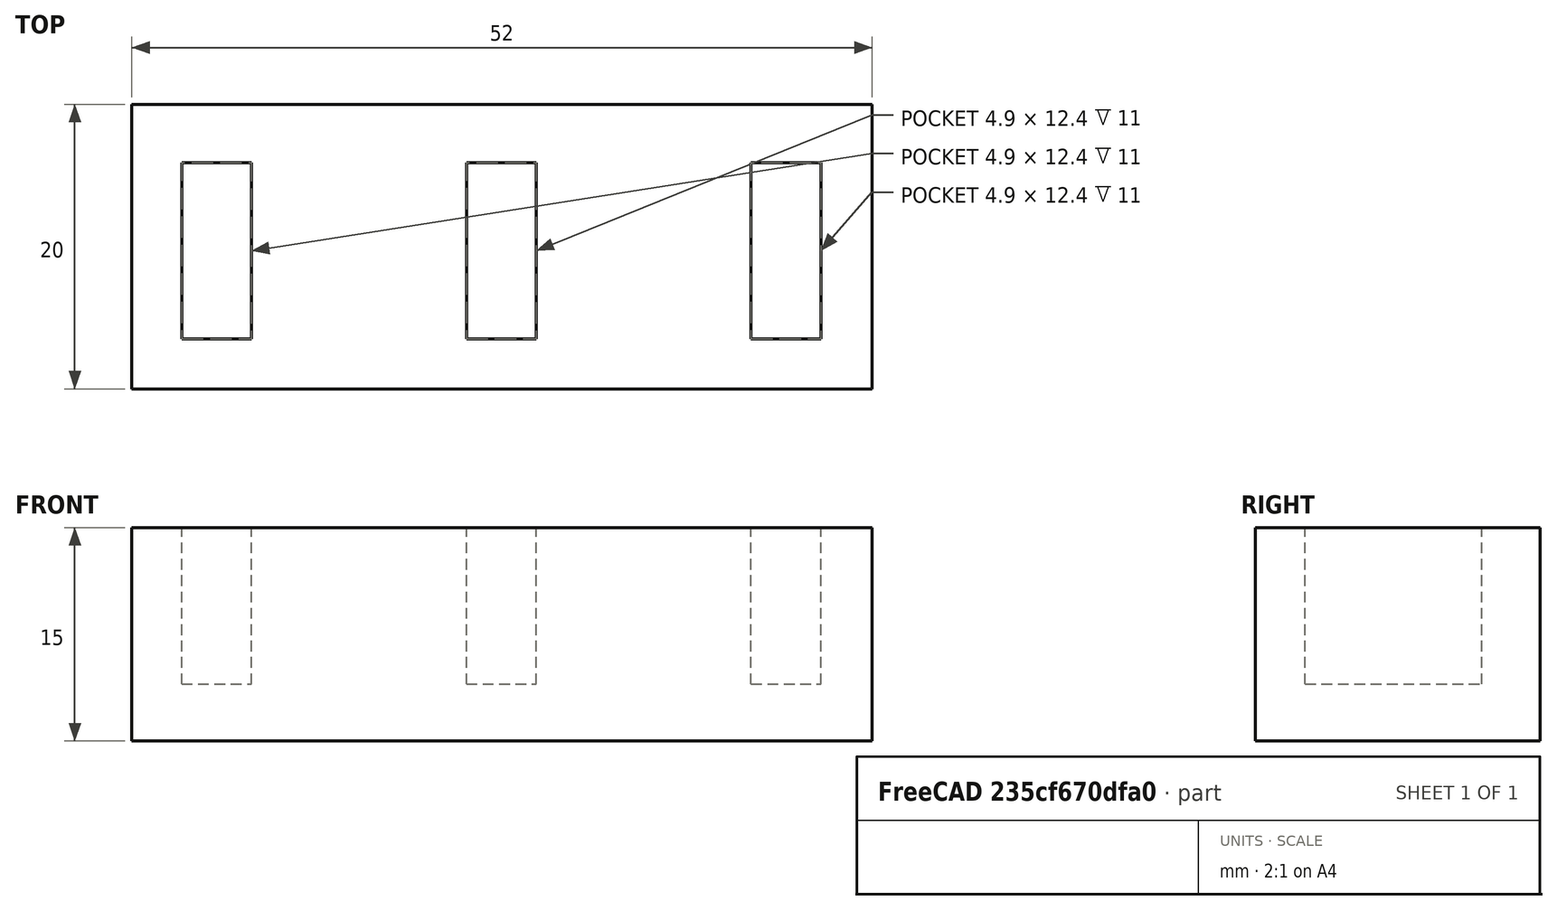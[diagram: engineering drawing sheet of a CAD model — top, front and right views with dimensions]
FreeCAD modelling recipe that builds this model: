
FCSTD DOCUMENT  (FreeCAD 0.16R6707 (Git))
Label: porta-pendrive
License: All rights reserved
LicenseURL: http://en.wikipedia.org/wiki/All_rights_reserved
objects: Part::Box×4, Part::MultiFuse×1, Part::Cut×1
note: 6 computed .brp shape members not serialized (recipe doc carries the construction recipe); baked Part::Feature solids carry a one-line shape summary decoded from their .brp

FEATURE [Part::Box] Box  label="base"
  Height = 15
  Length = 52
  Width = 20
FEATURE [Part::Box] Box001  label="slot1"
  Height = 20
  Length = 4.9
  Placement = pos=(3.5,3.5,4) rot=(0,0,1;0rad)
  Width = 12.4
FEATURE [Part::Box] Box002  label="slot002"
  Height = 20
  Length = 4.9
  Placement = pos=(23.5,3.5,4) rot=(0,0,1;0rad)
  Width = 12.4
FEATURE [Part::Box] Box003  label="slot003"
  Height = 20
  Length = 4.9
  Placement = pos=(43.5,3.5,4) rot=(0,0,1;0rad)
  Width = 12.4
FEATURE [Part::MultiFuse] Fusion  label="slots"
  Shapes = -> [Box001,Box003,Box002]
FEATURE [Part::Cut] Cut  label="objeto-final"
  Base = -> Box
  Tool = -> Fusion
